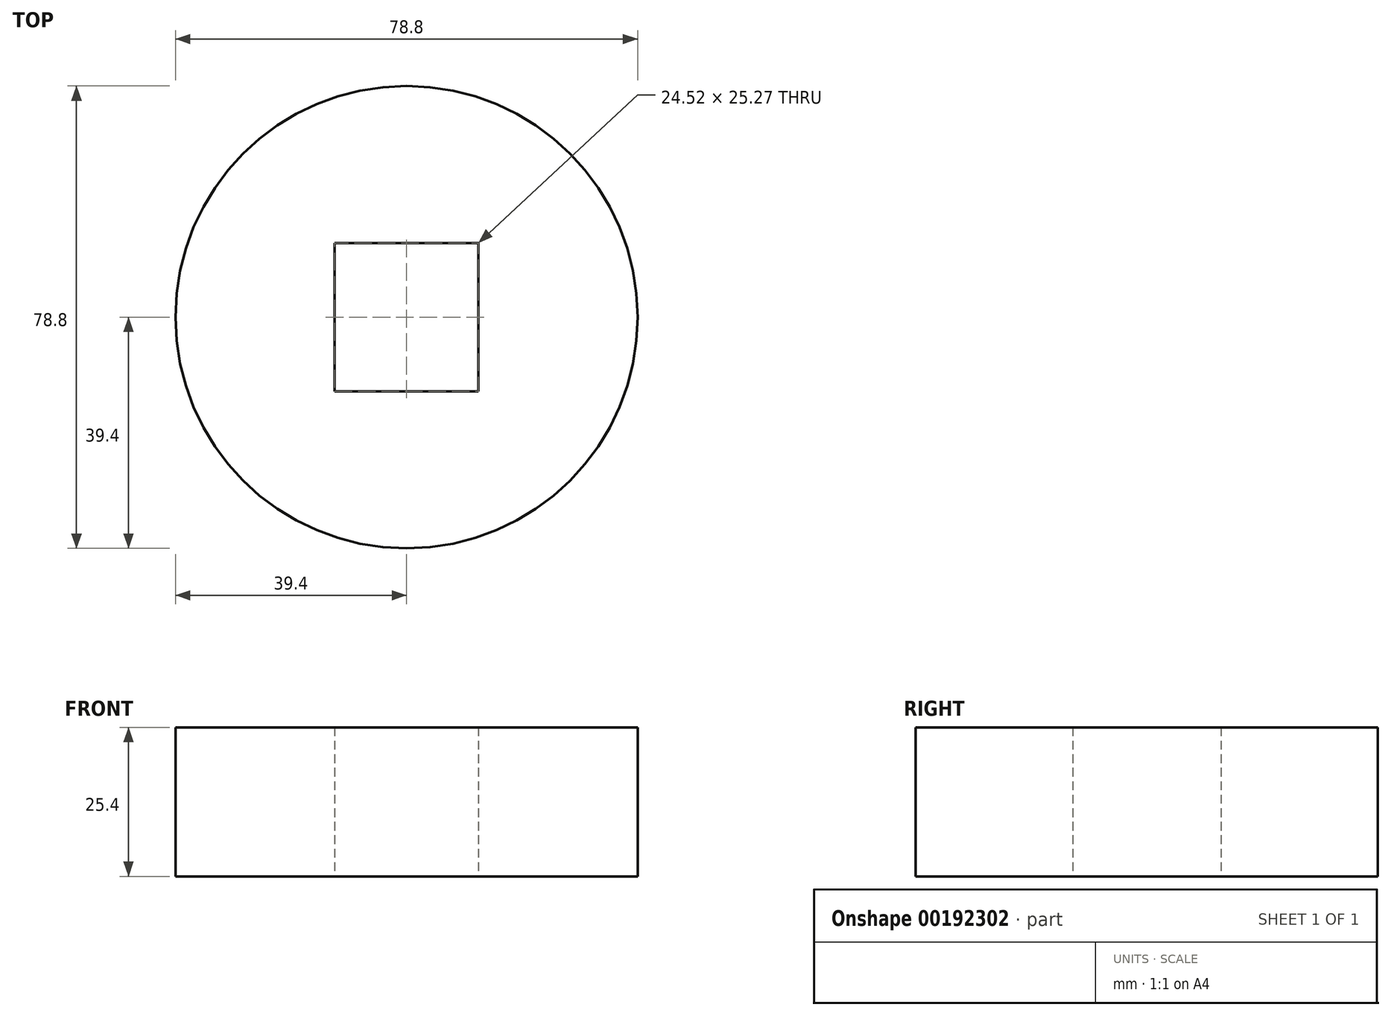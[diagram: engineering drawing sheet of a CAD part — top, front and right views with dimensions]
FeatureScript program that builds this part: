
annotation { "Feature Type Name" : "Feature", "Feature Type Description" : "" }
export const myFeature = defineFeature(function(context is Context, id is Id, definition is map)
    precondition{}
    {
        {
            var Q0;
            Q0=qCreatedBy(makeId("Top.planeOp"),FACE);
            var sketch = newSketch(context, id + "F0", { "sketchPlane" : qUnion([Q0])});
            skCircle(sketch, "E0", {"center": v(0, 0) * mm, "radius": 39.4 * mm});
            skLineSegment(sketch, "E1.bottom", {"start": v(0, 0) * mm, "end": v(-12.26, 0) * mm});
            skLineSegment(sketch, "E1.top", {"start": v(0, -12.64) * mm, "end": v(-12.26, -12.64) * mm});
            skLineSegment(sketch, "E1.left", {"start": v(0, 0) * mm, "end": v(0, -12.64) * mm});
            skLineSegment(sketch, "E1.right", {"start": v(-12.26, 0) * mm, "end": v(-12.26, -12.64) * mm});
            skLineSegment(sketch, "E2.MirrorCS", {"start": v(-12.26, 0) * mm, "end": v(-12.26, 12.64) * mm});
            skLineSegment(sketch, "E3.MirrorCS", {"start": v(0, 12.64) * mm, "end": v(-12.26, 12.64) * mm});
            skLineSegment(sketch, "E4.MirrorCS", {"start": v(0, 0) * mm, "end": v(12.26, 0) * mm});
            skLineSegment(sketch, "E5.MirrorCS", {"start": v(12.26, 0) * mm, "end": v(12.26, 12.64) * mm});
            skLineSegment(sketch, "E6.MirrorCS", {"start": v(0, 12.64) * mm, "end": v(12.26, 12.64) * mm});
            skLineSegment(sketch, "E7.MirrorCS", {"start": v(12.26, 0) * mm, "end": v(12.26, -12.64) * mm});
            skLineSegment(sketch, "E8.MirrorCS", {"start": v(0, -12.64) * mm, "end": v(12.26, -12.64) * mm});
            skSolve(sketch);
        }
        {
            var Q0;
            Q0 = qSketchRegion(id + "F0", true);
            extrude(context, id + "F1", {"entities" : qUnion([Q0]), "depth" : 25.4 * mm});
        }
    });
